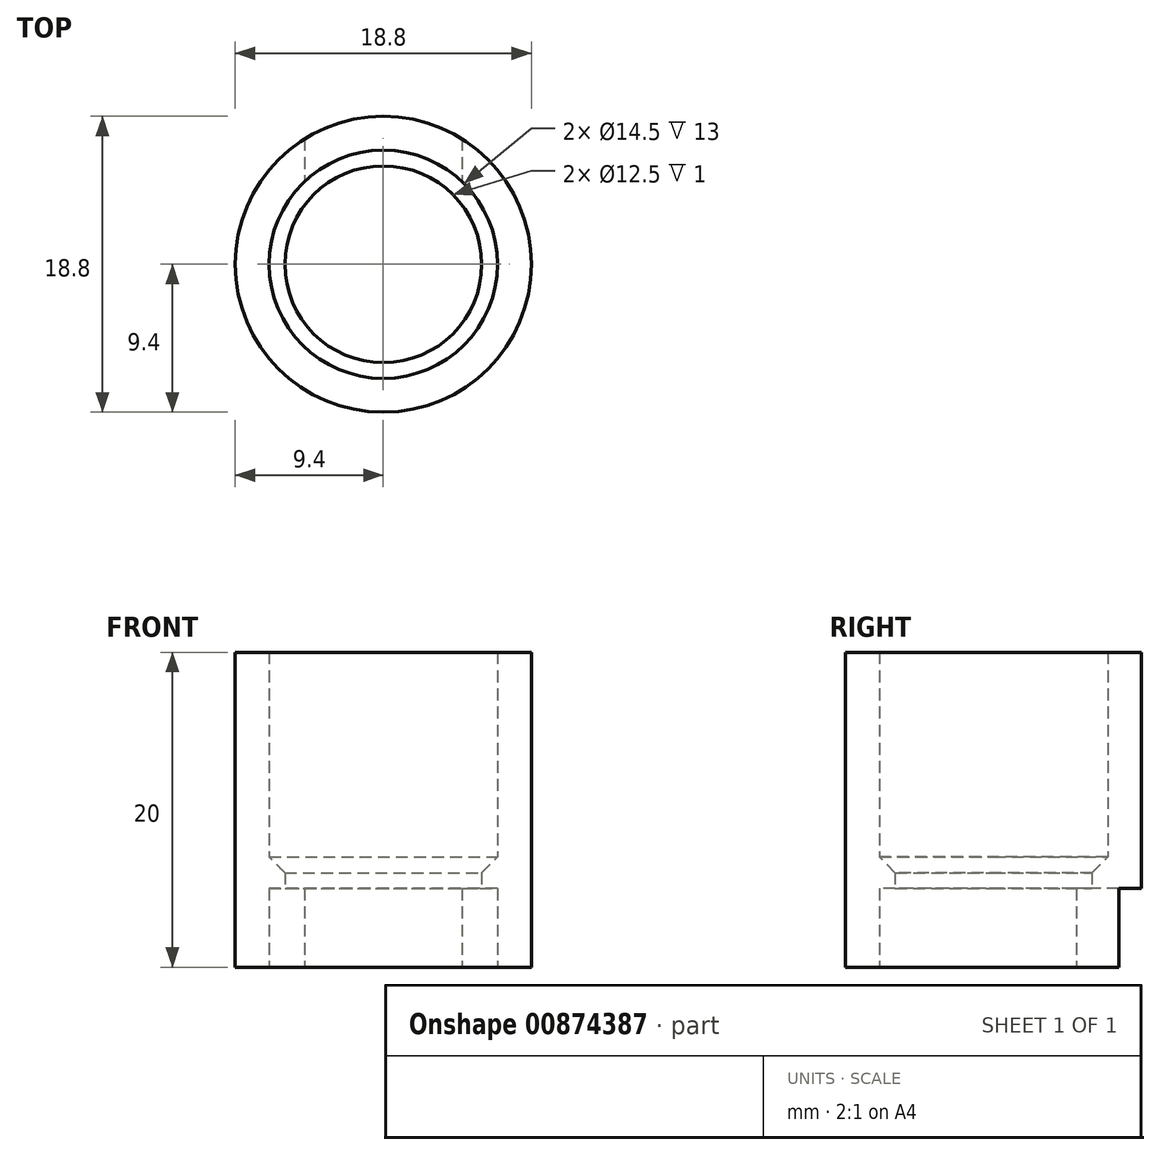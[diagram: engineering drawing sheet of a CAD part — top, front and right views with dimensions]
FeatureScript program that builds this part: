
annotation { "Feature Type Name" : "Feature", "Feature Type Description" : "" }
export const myFeature = defineFeature(function(context is Context, id is Id, definition is map)
    precondition{}
    {
        {
            var Q0;
            Q0=qCreatedBy(makeId("Front.planeOp"),FACE);
            var sketch = newSketch(context, id + "F0", { "sketchPlane" : qUnion([Q0])});
            skLineSegment(sketch, "E0", {"start": v(9.4, 0) * mm, "end": v(9.4, 20) * mm});
            skLineSegment(sketch, "E1", {"start": v(9.4, 20) * mm, "end": v(7.25, 20) * mm});
            skLineSegment(sketch, "E2", {"start": v(0, 0) * mm, "end": v(0, 10) * mm, "construction": true});
            skLineSegment(sketch, "E3", {"start": v(7.25, 20) * mm, "end": v(7.25, 7) * mm});
            skLineSegment(sketch, "E4", {"start": v(7.25, 0) * mm, "end": v(9.4, 0) * mm});
            skLineSegment(sketch, "E5", {"start": v(7.25, 5) * mm, "end": v(6.25, 5) * mm});
            skLineSegment(sketch, "E6", {"start": v(6.25, 5) * mm, "end": v(6.25, 6) * mm});
            skLineSegment(sketch, "E7", {"start": v(6.25, 6) * mm, "end": v(7.25, 7) * mm});
            skLineSegment(sketch, "E8.trimOffspring", {"start": v(7.25, 5) * mm, "end": v(7.25, 0) * mm});
            skSolve(sketch);
        }
        {
            var Q0;
            Q0=qSketchRegion(id+"F0",true);
            var Q1;
            Q1=sQuery(id+"F0.wireOp",EDGE,"E2");
            revolve(context, id + "F1", {"surfaceOperationType" : NewSurfaceOperationType.NEW, "entities" : qUnion([Q0]), "axis" : qUnion([Q1]), "revolveType" : RevolveType.FULL});
        }
        {
            var Q0;
            Q0=qCreatedBy(makeId("Front.planeOp"),FACE);
            var sketch = newSketch(context, id + "F2", { "sketchPlane" : qUnion([Q0])});
            skLineSegment(sketch, "E9.top", {"start": v(-5, 5) * mm, "end": v(5, 5) * mm});
            skLineSegment(sketch, "E9.left", {"start": v(-5, 0) * mm, "end": v(-5, 5) * mm});
            skLineSegment(sketch, "E9.right", {"start": v(5, 0) * mm, "end": v(5, 5) * mm});
            skLineSegment(sketch, "E10", {"start": v(-5, 0) * mm, "end": v(0, 0) * mm});
            skLineSegment(sketch, "E11", {"start": v(0, 0) * mm, "end": v(5, 0) * mm});
            skSolve(sketch);
        }
        {
            var Q0;
            Q0=qSketchRegion(id+"F2",true);
            extrude(context, id + "F3", {"entities" : qUnion([Q0]), "operationType" : NewBodyOperationType.REMOVE, "oppositeDirection" : true, "depth" : 25 * mm, "offsetDistance" : 25 * mm});
        }
        {
            var Q0;
            Q0=makeQuery(id+"F3.boolean.opBoolean","MERGE",FACE,{"derivedFrom":[makeQuery(id+"F1.opRevolve","SWEPT_FACE",FACE,{"disambiguationData":[OSD([sQuery(id+"F0.wireOp",EDGE,"4d8A3SZY-SQrE-TdKS-csu8-dthYd3GXM32D")])]})],"fromTools":[makeQuery(id+"F3.opExtrude","SWEPT_FACE",FACE,{"disambiguationData":[OSD([sQuery(id+"F2.wireOp",EDGE,"E9.top")])]})]});
            cPlane(context, id + "F4", {"entities" : qUnion([Q0]), "cplaneType" : CPlaneType.OFFSET, "offset" : 2 * mm, "oppositeDirection" : true, "width" : 150 * mm, "height" : 150 * mm});
        }
    });
